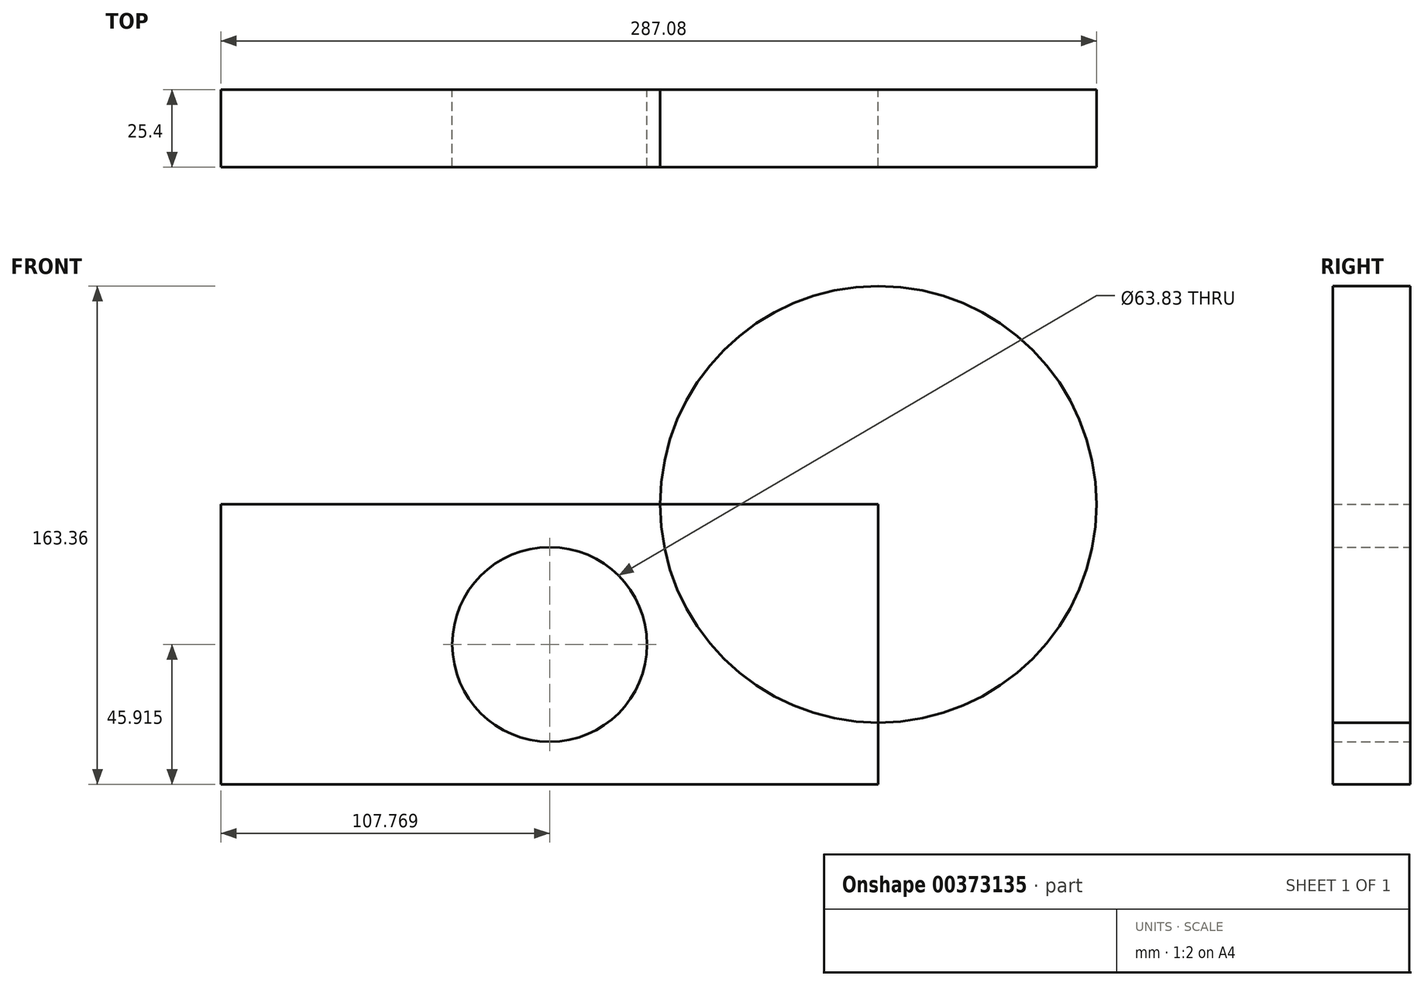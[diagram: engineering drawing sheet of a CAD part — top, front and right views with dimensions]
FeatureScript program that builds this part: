
annotation { "Feature Type Name" : "Feature", "Feature Type Description" : "" }
export const myFeature = defineFeature(function(context is Context, id is Id, definition is map)
    precondition{}
    {
        {
            var Q0;
            Q0=qCreatedBy(makeId("Front.planeOp"),FACE);
            var sketch = newSketch(context, id + "F0", { "sketchPlane" : qUnion([Q0])});
            skLineSegment(sketch, "E0.bottom", {"start": v(-14.69, 11.8) * mm, "end": v(-230.23, 11.8) * mm});
            skLineSegment(sketch, "E0.top", {"start": v(-14.69, -80.03) * mm, "end": v(-230.23, -80.03) * mm});
            skLineSegment(sketch, "E0.left", {"start": v(-14.69, 11.8) * mm, "end": v(-14.69, -80.03) * mm});
            skLineSegment(sketch, "E0.right", {"start": v(-230.23, 11.8) * mm, "end": v(-230.23, -80.03) * mm});
            skPoint(sketch, "E0.middle", {"position": v(-122.46, -34.12) * mm});
            skCircle(sketch, "E1", {"center": v(-14.69, 11.8) * mm, "radius": 71.54 * mm});
            skCircle(sketch, "E2", {"center": v(-122.46, -34.12) * mm, "radius": 31.91 * mm});
            skSolve(sketch);
        }
        {
            var Q0;
            {var subQ2=sQuery(id+"F0.wireOp",EDGE,"E0.top");Q0=makeQuery(id+"F0.imprint","IMPRINT",FACE,{"disambiguationData":[TD([[makeQuery(id+"F0.imprint","IMPRINT",EDGE,{"derivedFrom":subQ2}),-1.0]])]});}
            var Q1;
            {var subQ0=sQuery(id+"F0.wireOp",EDGE,"E0.left");var subQ1=sQuery(id+"F0.wireOp",EDGE,"E0.bottom");var subQ2=makeQuery(id+"F0.imprint","INTERSECT",VERTEX,{"derivedFrom":[subQ1,subQ0]});Q1=makeQuery(id+"F0.imprint","IMPRINT",FACE,{"disambiguationData":[TD([[makeQuery(id+"F0.imprint","IMPRINT",EDGE,{"disambiguationData":[TD([[subQ2,-1.0]])],"derivedFrom":subQ1}),-1.0]])]});}
            extrude(context, id + "F1", {"entities" : qUnion([Q0, Q1]), "depth" : 25.4 * mm});
        }
    });
